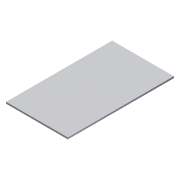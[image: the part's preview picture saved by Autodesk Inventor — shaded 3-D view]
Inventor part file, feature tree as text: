
AUTODESK INVENTOR PART (.ipt)
format: ipt  version: 2014 (Build 180170000, 170)  size: 67,584 bytes
history: native  units: mm
features: extrude x1, sketch x1
ambient origin geometry x8: Origin, YZ Plane, XZ Plane, XY Plane, X Axis, Y Axis, Z Axis, Center Point
bodies: Solid1 (feature_tree)
feature tree (2):
  extrude  "Extrusion1"  Depth=110.0mm
  sketch  "Sketch1"  dims[d0=189.0mm d1=110.0mm d2=3.0mm d3=0.0mm]
